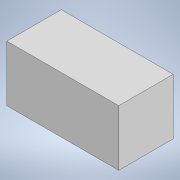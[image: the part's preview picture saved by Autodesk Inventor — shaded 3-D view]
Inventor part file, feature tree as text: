
AUTODESK INVENTOR PART (.ipt)
format: ipt  version: 2020 (Build 240168000, 168)  size: 87,040 bytes
history: native  units: mm
features: other x1, extrude x1, sketch x1
ambient origin geometry x8: Origin, YZ Plane, XZ Plane, XY Plane, X Axis, Y Axis, Z Axis, Center Point
bodies: Body1 (feature_tree)
feature tree (3):
  other  "Bryła1"
  extrude  "Wyciągnięcie proste1"  Depth=74.0mm
  sketch  "Szkic1"
